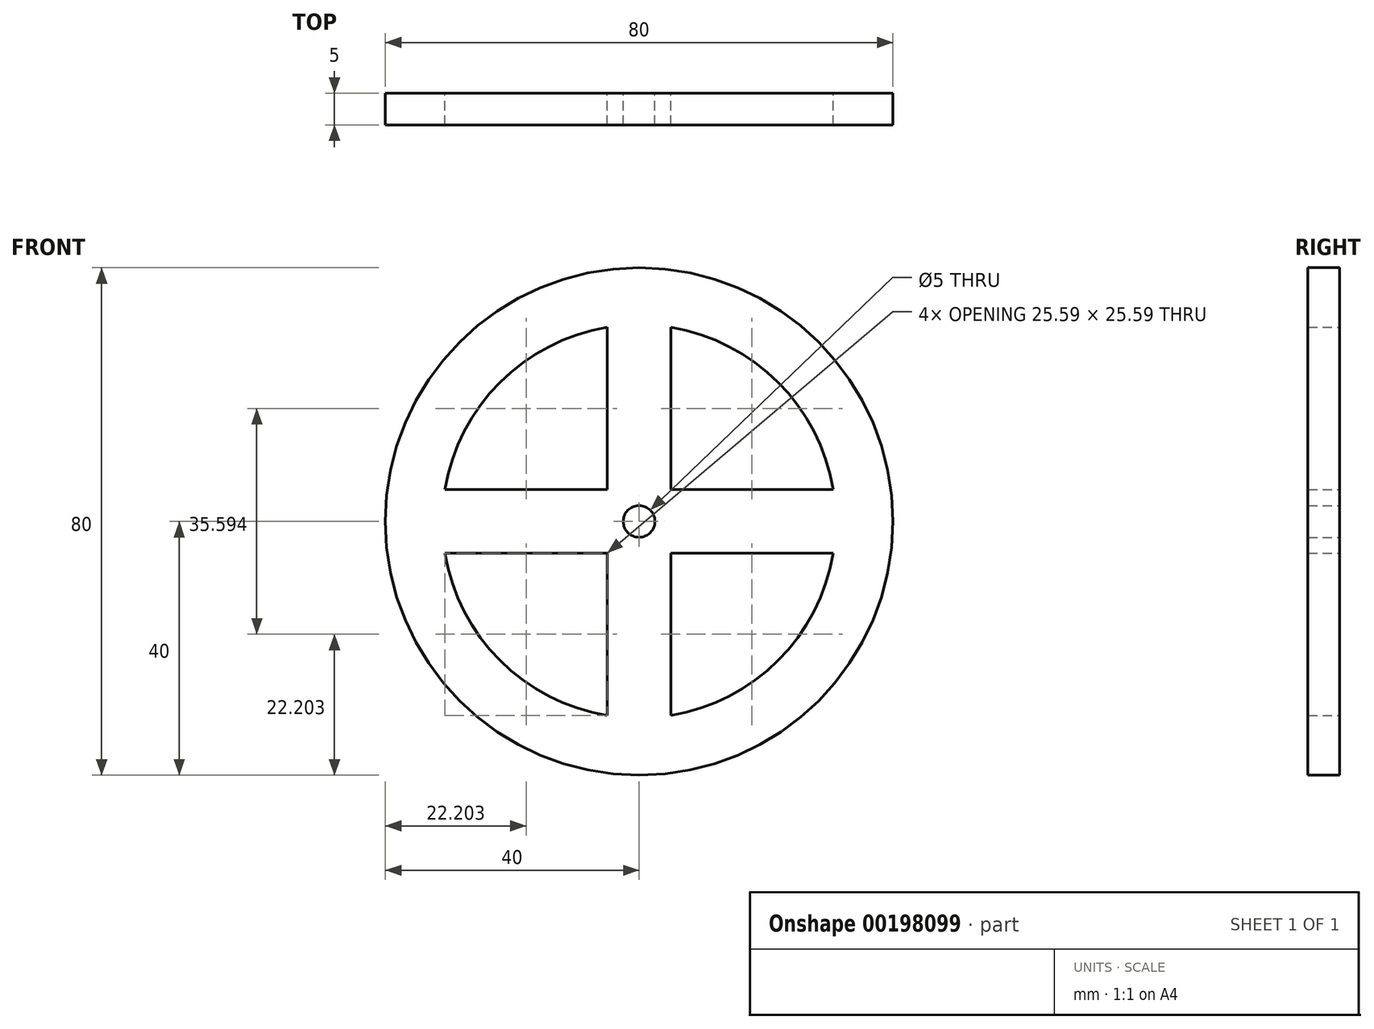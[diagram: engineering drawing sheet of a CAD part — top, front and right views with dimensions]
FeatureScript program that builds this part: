
annotation { "Feature Type Name" : "Feature", "Feature Type Description" : "" }
export const myFeature = defineFeature(function(context is Context, id is Id, definition is map)
    precondition{}
    {
        {
            var Q0;
            Q0=qCreatedBy(makeId("Front.planeOp"),FACE);
            var sketch = newSketch(context, id + "F0", { "sketchPlane" : qUnion([Q0])});
            skCircle(sketch, "E0", {"center": v(0, 0) * mm, "radius": 40 * mm});
            skArc(sketch, "E1", {"start": v(-5, 30.6) * mm, "mid": v(-21.92, 21.92) * mm, "end": v(-30.6, 5) * mm});
            skArc(sketch, "E2", {"start": v(5, -5.6) * mm, "mid": v(5.3, -5.3) * mm, "end": v(5.6, -5) * mm});
            skCircle(sketch, "E3", {"center": v(0, 0) * mm, "radius": 2.5 * mm});
            skLineSegment(sketch, "E4", {"start": v(0, 0) * mm, "end": v(0, 31) * mm, "construction": true});
            skLineSegment(sketch, "E5", {"start": v(0, 0) * mm, "end": v(2.5, 0) * mm});
            skLineSegment(sketch, "E6", {"start": v(0, 0) * mm, "end": v(0, -31) * mm, "construction": true});
            skLineSegment(sketch, "E7", {"start": v(0, 0) * mm, "end": v(-31, 0) * mm, "construction": true});
            skLineSegment(sketch, "E8.0", {"start": v(5, 5) * mm, "end": v(5, 30.6) * mm});
            skLineSegment(sketch, "E9.0", {"start": v(-5, -5) * mm, "end": v(-30.6, -5) * mm});
            skLineSegment(sketch, "E10.0", {"start": v(-5, 5) * mm, "end": v(-5, 30.6) * mm});
            skLineSegment(sketch, "E11.0", {"start": v(5, -5) * mm, "end": v(30.6, -5) * mm});
            skLineSegment(sketch, "E12.0", {"start": v(5, 5) * mm, "end": v(30.6, 5) * mm});
            skLineSegment(sketch, "E13.0", {"start": v(-5, 5) * mm, "end": v(-30.6, 5) * mm});
            skLineSegment(sketch, "E14.0", {"start": v(-5, -5) * mm, "end": v(-5, -30.6) * mm});
            skLineSegment(sketch, "E15.0", {"start": v(5, -5) * mm, "end": v(5, -30.6) * mm});
            skArc(sketch, "E16.trimOffspring", {"start": v(-30.6, -5) * mm, "mid": v(-21.92, -21.92) * mm, "end": v(-5, -30.6) * mm});
            skArc(sketch, "E17.trimOffspring", {"start": v(5, -30.6) * mm, "mid": v(21.92, -21.92) * mm, "end": v(30.6, -5) * mm});
            skArc(sketch, "E18.trimOffspring", {"start": v(-5.6, -5) * mm, "mid": v(-5.3, -5.3) * mm, "end": v(-5, -5.6) * mm});
            skArc(sketch, "E19.trimOffspring", {"start": v(-5, 5.6) * mm, "mid": v(-5.3, 5.3) * mm, "end": v(-5.6, 5) * mm});
            skArc(sketch, "E20.trimOffspring", {"start": v(5.6, 5) * mm, "mid": v(5.3, 5.3) * mm, "end": v(5, 5.6) * mm});
            skLineSegment(sketch, "E21", {"start": v(2.5, 0) * mm, "end": v(0, 0) * mm});
            skLineSegment(sketch, "E22", {"start": v(0, 0) * mm, "end": v(31, 0) * mm, "construction": true});
            skArc(sketch, "E23.trimOffspring", {"start": v(30.6, 5) * mm, "mid": v(21.92, 21.92) * mm, "end": v(5, 30.6) * mm});
            skSolve(sketch);
        }
        {
            var Q0;
            Q0=makeQuery(id+"F0.imprint","IMPRINT",FACE,{"disambiguationData":[TD([[makeQuery(id+"F0.imprint","IMPRINT",EDGE,{"derivedFrom":sQuery(id+"F0.wireOp",EDGE,"E0")}),1.0]])]});
            extrude(context, id + "F1", {"entities" : qUnion([Q0]), "endBound" : BoundingType.SYMMETRIC, "depth" : 5 * mm});
        }
    });
